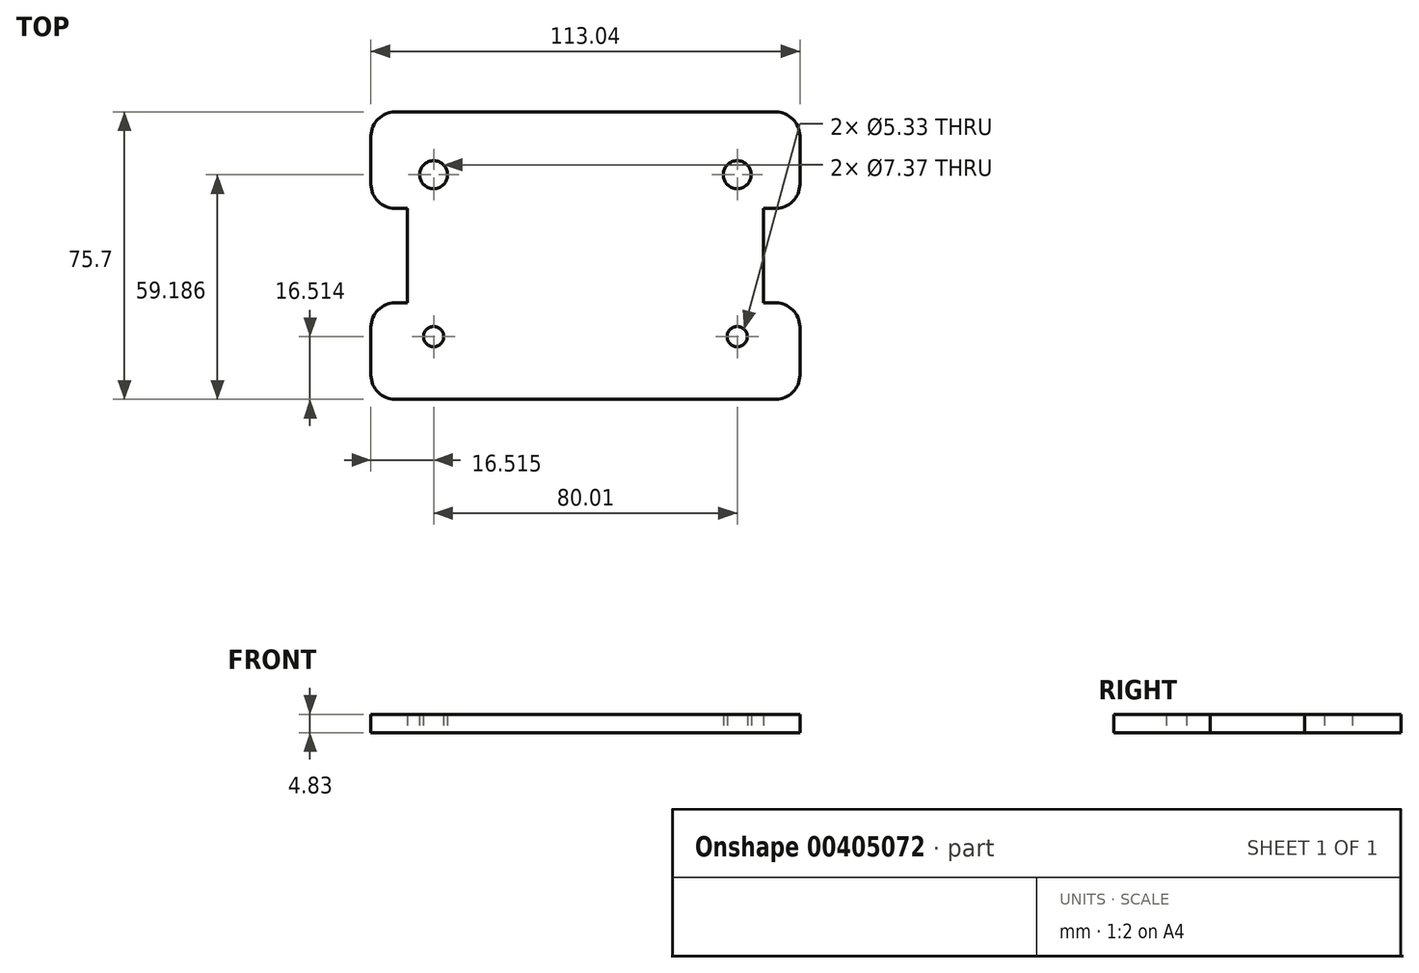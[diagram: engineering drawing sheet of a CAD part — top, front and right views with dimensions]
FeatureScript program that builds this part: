
annotation { "Feature Type Name" : "Feature", "Feature Type Description" : "" }
export const myFeature = defineFeature(function(context is Context, id is Id, definition is map)
    precondition{}
    {
        {
            var Q0;
            Q0=qCreatedBy(makeId("Top.planeOp"),FACE);
            var sketch = newSketch(context, id + "F0", { "sketchPlane" : qUnion([Q0])});
            skLineSegment(sketch, "E0.bottom", {"start": v(-50.16, 37.85) * mm, "end": v(50.17, 37.85) * mm});
            skLineSegment(sketch, "E0.top", {"start": v(-50.17, -37.85) * mm, "end": v(50.16, -37.85) * mm});
            skLineSegment(sketch, "E0.left", {"start": v(-56.52, 31.5) * mm, "end": v(-56.52, 18.8) * mm});
            skLineSegment(sketch, "E0.right", {"start": v(56.52, 31.5) * mm, "end": v(56.52, 18.8) * mm});
            skPoint(sketch, "E0.middle", {"position": v(0, 0) * mm});
            skLineSegment(sketch, "E1.bottom", {"start": v(-50.16, 12.45) * mm, "end": v(-46.86, 12.45) * mm});
            skLineSegment(sketch, "E1.top", {"start": v(-50.17, -12.45) * mm, "end": v(-46.86, -12.45) * mm});
            skLineSegment(sketch, "E1.right", {"start": v(-46.86, 12.45) * mm, "end": v(-46.86, -12.45) * mm});
            skLineSegment(sketch, "E2.MirrorCS", {"start": v(50.17, 12.45) * mm, "end": v(46.86, 12.45) * mm});
            skLineSegment(sketch, "E3.MirrorCS", {"start": v(46.86, 12.45) * mm, "end": v(46.86, -12.45) * mm});
            skLineSegment(sketch, "E4.MirrorCS", {"start": v(50.16, -12.45) * mm, "end": v(46.86, -12.45) * mm});
            skCircle(sketch, "E5", {"center": v(-40, -21.34) * mm, "radius": 2.67 * mm});
            skCircle(sketch, "E6", {"center": v(-40, 21.34) * mm, "radius": 3.68 * mm});
            skCircle(sketch, "E7.MirrorC", {"center": v(40, 21.34) * mm, "radius": 3.68 * mm});
            skCircle(sketch, "E8.MirrorC", {"center": v(40, -21.34) * mm, "radius": 2.67 * mm});
            skLineSegment(sketch, "E9.trimOffspring", {"start": v(-56.52, -18.8) * mm, "end": v(-56.52, -31.5) * mm});
            skLineSegment(sketch, "E10.trimOffspring", {"start": v(56.52, -18.8) * mm, "end": v(56.52, -31.5) * mm});
            skPoint(sketch, "E11.visualSharp", {"position": v(-56.52, 37.85) * mm});
            skArc(sketch, "E11.filletArc", {"start": v(-50.16, 37.85) * mm, "mid": v(-54.66, 35.99) * mm, "end": v(-56.52, 31.5) * mm});
            skPoint(sketch, "E12.visualSharp", {"position": v(56.52, 37.85) * mm});
            skArc(sketch, "E12.filletArc", {"start": v(56.52, 31.5) * mm, "mid": v(54.66, 35.99) * mm, "end": v(50.17, 37.85) * mm});
            skPoint(sketch, "E13.visualSharp", {"position": v(56.52, -37.85) * mm});
            skArc(sketch, "E13.filletArc", {"start": v(50.16, -37.85) * mm, "mid": v(54.66, -35.99) * mm, "end": v(56.52, -31.5) * mm});
            skPoint(sketch, "E14.visualSharp", {"position": v(-56.52, -37.85) * mm});
            skArc(sketch, "E14.filletArc", {"start": v(-56.52, -31.5) * mm, "mid": v(-54.66, -35.99) * mm, "end": v(-50.17, -37.85) * mm});
            skPoint(sketch, "E15.visualSharp", {"position": v(-56.52, -12.45) * mm});
            skArc(sketch, "E15.filletArc", {"start": v(-50.17, -12.45) * mm, "mid": v(-54.66, -14.3) * mm, "end": v(-56.52, -18.8) * mm});
            skPoint(sketch, "E16.visualSharp", {"position": v(-56.52, 12.45) * mm});
            skArc(sketch, "E16.filletArc", {"start": v(-56.52, 18.8) * mm, "mid": v(-54.66, 14.3) * mm, "end": v(-50.16, 12.45) * mm});
            skPoint(sketch, "E17.visualSharp", {"position": v(56.52, 12.45) * mm});
            skArc(sketch, "E17.filletArc", {"start": v(50.17, 12.45) * mm, "mid": v(54.66, 14.3) * mm, "end": v(56.52, 18.8) * mm});
            skPoint(sketch, "E18.visualSharp", {"position": v(56.52, -12.45) * mm});
            skArc(sketch, "E18.filletArc", {"start": v(56.52, -18.8) * mm, "mid": v(54.66, -14.3) * mm, "end": v(50.16, -12.45) * mm});
            skSolve(sketch);
        }
        {
            var Q0;
            Q0=makeQuery(id+"F0.imprint","IMPRINT",FACE,{"disambiguationData":[TD([[makeQuery(id+"F0.imprint","IMPRINT",EDGE,{"derivedFrom":sQuery(id+"F0.wireOp",EDGE,"E0.bottom")}),-1.0]])]});
            extrude(context, id + "F1", {"entities" : qUnion([Q0]), "depth" : 4.83 * mm});
        }
    });
